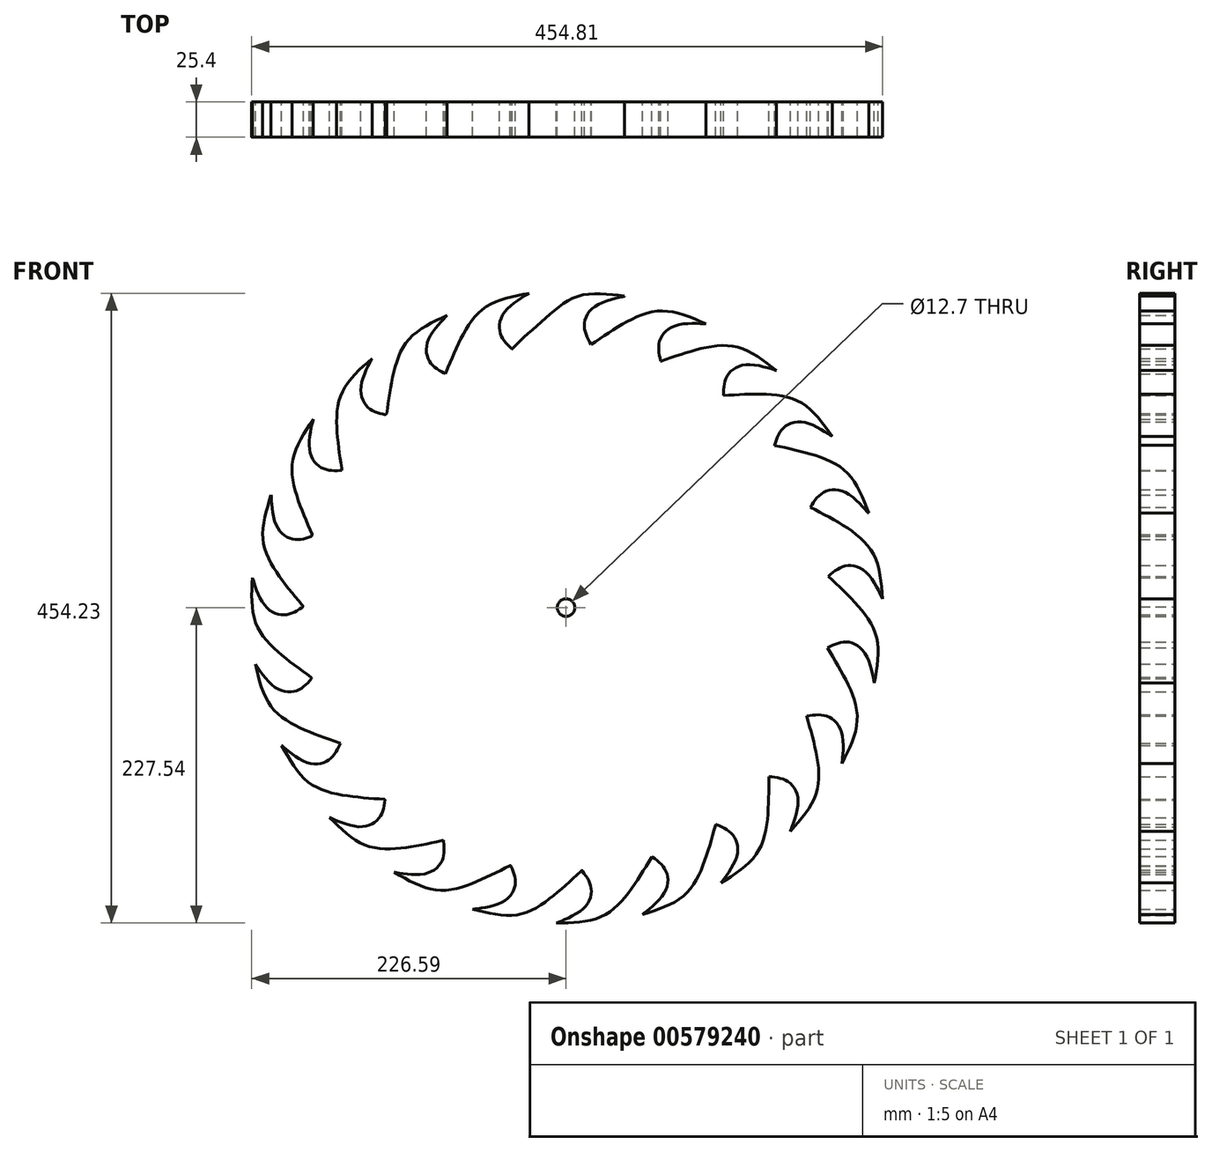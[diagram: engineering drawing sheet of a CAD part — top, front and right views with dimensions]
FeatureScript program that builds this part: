
annotation { "Feature Type Name" : "Feature", "Feature Type Description" : "" }
export const myFeature = defineFeature(function(context is Context, id is Id, definition is map)
    precondition{}
    {
        {
            var Q0;
            Q0=qCreatedBy(makeId("Front.planeOp"),FACE);
            var sketch = newSketch(context, id + "F0", { "sketchPlane" : qUnion([Q0])});
            skCircle(sketch, "E0", {"center": v(0, 0) * mm, "radius": 190.5 * mm});
            skFitSpline(sketch, "E1", {"points": [v(18.12, 189.64) * mm, v(13.24, 202.8) * mm, v(22.46, 218.16) * mm, v(42.19, 224.67) * mm, v(41.34, 224.83) * mm], "startDerivative": vector(-24.64, 44.24) * mm, "endDerivative": vector(-11.68, 1.02) * mm});
            skFitSpline(sketch, "E2", {"points": [v(42.19, 224.67) * mm, v(8.88, 224.67) * mm, v(-15.84, 207.72) * mm, v(-38.7, 186.53) * mm], "startDerivative": vector(-98.7, 12.3) * mm, "endDerivative": vector(-57.4, -63.42) * mm});
            skFitSpline(sketch, "E3", {"points": [v(68.28, 177.66) * mm, v(67.32, 191.67) * mm, v(80.5, 203.8) * mm, v(100.8, 204.7) * mm, v(100.51, 204.86) * mm], "startDerivative": vector(-11.13, 49.4) * mm, "endDerivative": vector(-10.91, 4.28) * mm});
            skFitSpline(sketch, "E4", {"points": [v(100.8, 204.7) * mm, v(69.4, 213.96) * mm, v(42.54, 205.38) * mm, v(18.12, 189.64) * mm], "startDerivative": vector(-91.19, 39.7) * mm, "endDerivative": vector(-72.22, -48.4) * mm});
            skFitSpline(sketch, "E5", {"points": [v(113.46, 153) * mm, v(116.04, 166.8) * mm, v(131.85, 175.23) * mm, v(151.72, 171.01) * mm, v(151.47, 171.23) * mm], "startDerivative": vector(1.62, 50.6) * mm, "endDerivative": vector(-9.49, 6.88) * mm});
            skFitSpline(sketch, "E6", {"points": [v(151.72, 171.01) * mm, v(123.65, 187.84) * mm, v(95.49, 186.28) * mm, v(68.28, 177.66) * mm], "startDerivative": vector(-78.31, 61.3) * mm, "endDerivative": vector(-82.05, -28.74) * mm});
            skFitSpline(sketch, "E7", {"points": [v(150.32, 116.92) * mm, v(156.7, 129.43) * mm, v(174.25, 133.05) * mm, v(192.12, 123.4) * mm, v(191.94, 123.67) * mm], "startDerivative": vector(15.86, 48.09) * mm, "endDerivative": vector(-7.16, 9.28) * mm});
            skFitSpline(sketch, "E8", {"points": [v(192.12, 123.4) * mm, v(169.95, 147.47) * mm, v(142.5, 153.94) * mm, v(113.46, 153) * mm], "startDerivative": vector(-57.79, 80.94) * mm, "endDerivative": vector(-86.83, -4.37) * mm});
            skFitSpline(sketch, "E9", {"points": [v(176.21, 72.44) * mm, v(185.57, 82.91) * mm, v(203.45, 81.95) * mm, v(218.28, 68.06) * mm, v(218.18, 68.38) * mm], "startDerivative": vector(27.57, 42.47) * mm, "endDerivative": vector(-4.56, 10.8) * mm});
            skFitSpline(sketch, "E10", {"points": [v(218.28, 68.06) * mm, v(202.97, 97) * mm, v(178.06, 110.22) * mm, v(150.32, 116.92) * mm], "startDerivative": vector(-35.3, 92.98) * mm, "endDerivative": vector(-85.08, 17.86) * mm});
            skFitSpline(sketch, "E11", {"points": [v(189.1, 22.5) * mm, v(201.03, 29.9) * mm, v(217.92, 23.93) * mm, v(228.22, 6.41) * mm, v(228.21, 6.74) * mm], "startDerivative": vector(38.45, 32.95) * mm, "endDerivative": vector(-1.32, 11.65) * mm});
            skFitSpline(sketch, "E12", {"points": [v(228.22, 6.41) * mm, v(221.7, 38.49) * mm, v(201.55, 58.22) * mm, v(176.21, 72.44) * mm], "startDerivative": vector(-7.57, 99.17) * mm, "endDerivative": vector(-76.56, 41.18) * mm});
            skFitSpline(sketch, "E13", {"points": [v(188.43, -28.96) * mm, v(201.84, -24.8) * mm, v(216.68, -34.81) * mm, v(222.26, -54.35) * mm, v(222.34, -54.03) * mm], "startDerivative": vector(45.48, 22.25) * mm, "endDerivative": vector(1.64, 11.6) * mm});
            skFitSpline(sketch, "E14", {"points": [v(222.26, -54.35) * mm, v(224, -21.67) * mm, v(209.44, 2.49) * mm, v(189.1, 22.5) * mm], "startDerivative": vector(17.54, 97.9) * mm, "endDerivative": vector(-63.79, 59.07) * mm});
            skFitSpline(sketch, "E15", {"points": [v(173.57, -78.3) * mm, v(187.84, -78.2) * mm, v(199.25, -92.02) * mm, v(199.07, -112.34) * mm, v(199.24, -112.05) * mm], "startDerivative": vector(49.92, 8.48) * mm, "endDerivative": vector(4.86, 10.67) * mm});
            skFitSpline(sketch, "E16", {"points": [v(199.07, -112.34) * mm, v(209.98, -81.48) * mm, v(202.85, -54.19) * mm, v(188.43, -28.96) * mm], "startDerivative": vector(44.5, 88.94) * mm, "endDerivative": vector(-44.49, 74.7) * mm});
            skFitSpline(sketch, "E17", {"points": [v(146.3, -121.93) * mm, v(159.9, -125.39) * mm, v(167.32, -141.7) * mm, v(161.85, -161.26) * mm, v(162.08, -161.03) * mm], "startDerivative": vector(50.4, -4.84) * mm, "endDerivative": vector(7.47, 9.03) * mm});
            skFitSpline(sketch, "E18", {"points": [v(161.85, -161.26) * mm, v(180.43, -134.32) * mm, v(180.67, -106.12) * mm, v(173.57, -78.3) * mm], "startDerivative": vector(66.17, 74.25) * mm, "endDerivative": vector(-23.45, 83.71) * mm});
            skFitSpline(sketch, "E19", {"points": [v(107.96, -156.42) * mm, v(120.04, -163.59) * mm, v(122.53, -181.33) * mm, v(111.75, -198.55) * mm, v(112.04, -198.39) * mm], "startDerivative": vector(46.98, -18.89) * mm, "endDerivative": vector(9.72, 6.55) * mm});
            skFitSpline(sketch, "E20", {"points": [v(111.75, -198.55) * mm, v(137.2, -177.96) * mm, v(145.4, -150.97) * mm, v(146.3, -121.93) * mm], "startDerivative": vector(84.46, 52.52) * mm, "endDerivative": vector(1.17, 86.93) * mm});
            skFitSpline(sketch, "E21", {"points": [v(62, -179.6) * mm, v(71.9, -189.56) * mm, v(69.86, -207.36) * mm, v(55.1, -221.33) * mm, v(55.43, -221.25) * mm], "startDerivative": vector(40.74, -30.07) * mm, "endDerivative": vector(11.05, 3.9) * mm});
            skFitSpline(sketch, "E22", {"points": [v(55.1, -221.33) * mm, v(84.9, -207.78) * mm, v(99.6, -183.7) * mm, v(107.96, -156.42) * mm], "startDerivative": vector(94.93, 29.65) * mm, "endDerivative": vector(22.94, 83.86) * mm});
            skFitSpline(sketch, "E23", {"points": [v(11.38, -189.46) * mm, v(18.05, -201.81) * mm, v(11.07, -218.31) * mm, v(-7.03, -227.54) * mm, v(-6.7, -227.55) * mm], "startDerivative": vector(30.58, -40.36) * mm, "endDerivative": vector(11.7, 0.62) * mm});
            skFitSpline(sketch, "E24", {"points": [v(-7.03, -227.54) * mm, v(25.38, -222.97) * mm, v(46.29, -204.04) * mm, v(62, -179.6) * mm], "startDerivative": vector(99.44, 1.6) * mm, "endDerivative": vector(45.7, 73.95) * mm});
            skFitSpline(sketch, "E25", {"points": [v(-39.94, -185.51) * mm, v(-36.63, -199.16) * mm, v(-47.58, -213.34) * mm, v(-67.43, -217.66) * mm, v(-67.12, -217.75) * mm], "startDerivative": vector(19.3, -46.8) * mm, "endDerivative": vector(11.48, -2.38) * mm});
            skFitSpline(sketch, "E26", {"points": [v(-67.43, -217.66) * mm, v(-34.92, -221.48) * mm, v(-9.89, -208.49) * mm, v(11.38, -189.46) * mm], "startDerivative": vector(96.58, -23.74) * mm, "endDerivative": vector(63.02, 59.9) * mm});
            skFitSpline(sketch, "E27", {"points": [v(-88.36, -167.76) * mm, v(-89.05, -181.79) * mm, v(-103.56, -192.3) * mm, v(-123.82, -190.82) * mm, v(-123.54, -191) * mm], "startDerivative": vector(5.29, -50.36) * mm, "endDerivative": vector(10.34, -5.53) * mm});
            skFitSpline(sketch, "E28", {"points": [v(-123.82, -190.82) * mm, v(-93.72, -203.68) * mm, v(-66.03, -198.3) * mm, v(-40.25, -186.06) * mm], "startDerivative": vector(85.93, -50.08) * mm, "endDerivative": vector(77.38, 39.64) * mm});
            skFitSpline(sketch, "E29", {"points": [v(-130.35, -137.99) * mm, v(-134.53, -151.4) * mm, v(-151.2, -157.92) * mm, v(-170.45, -151.42) * mm, v(-170.23, -151.66) * mm], "startDerivative": vector(-7.52, -50.07) * mm, "endDerivative": vector(8.62, -7.94) * mm});
            skFitSpline(sketch, "E30", {"points": [v(-170.45, -151.42) * mm, v(-144.54, -171.4) * mm, v(-116.39, -173.15) * mm, v(-88.36, -167.76) * mm], "startDerivative": vector(70.62, -70.03) * mm, "endDerivative": vector(84.84, 18.96) * mm});
            skFitSpline(sketch, "E31", {"points": [v(-162.75, -97.86) * mm, v(-170.55, -109.54) * mm, v(-188.4, -111.09) * mm, v(-205.02, -99.4) * mm, v(-204.87, -99.7) * mm], "startDerivative": vector(-21.36, -45.9) * mm, "endDerivative": vector(6.02, -10.06) * mm});
            skFitSpline(sketch, "E32", {"points": [v(-205.02, -99.4) * mm, v(-185.81, -125.91) * mm, v(-159.3, -135.53) * mm, v(-130.9, -138.3) * mm], "startDerivative": vector(47.94, -87.14) * mm, "endDerivative": vector(86.74, -5.8) * mm});
            skFitSpline(sketch, "E33", {"points": [v(-182.85, -50.48) * mm, v(-193.45, -59.7) * mm, v(-211.07, -56.5) * mm, v(-224.04, -40.86) * mm, v(-223.98, -41.19) * mm], "startDerivative": vector(-32.68, -38.68) * mm, "endDerivative": vector(3.17, -11.28) * mm});
            skFitSpline(sketch, "E34", {"points": [v(-224.04, -40.86) * mm, v(-212.48, -71.48) * mm, v(-189.43, -87.73) * mm, v(-162.75, -97.86) * mm], "startDerivative": vector(23.36, -96.68) * mm, "endDerivative": vector(82.17, -28.4) * mm});
            skFitSpline(sketch, "E35", {"points": [v(-189.38, 0.68) * mm, v(-202.14, -5.17) * mm, v(-218.15, 2.88) * mm, v(-226.17, 21.55) * mm, v(-226.2, 21.22) * mm], "startDerivative": vector(-42.28, -27.86) * mm, "endDerivative": vector(-0.15, -11.72) * mm});
            skFitSpline(sketch, "E36", {"points": [v(-226.17, 21.55) * mm, v(-223.73, -11.1) * mm, v(-206.21, -33.2) * mm, v(-183.48, -50.45) * mm], "startDerivative": vector(-4.93, -99.33) * mm, "endDerivative": vector(70.8, -50.46) * mm});
            skFitSpline(sketch, "E37", {"points": [v(-182.26, 51.65) * mm, v(-196.08, 49.2) * mm, v(-209.55, 61) * mm, v(-212.63, 81.09) * mm, v(-212.75, 80.78) * mm], "startDerivative": vector(-47.92, -16.37) * mm, "endDerivative": vector(-3.09, -11.3) * mm});
            skFitSpline(sketch, "E38", {"points": [v(-212.63, 81.09) * mm, v(-218.46, 48.88) * mm, v(-207.05, 23.09) * mm, v(-189.38, 0.68) * mm], "startDerivative": vector(-29.69, -94.92) * mm, "endDerivative": vector(55.87, -66.6) * mm});
            skFitSpline(sketch, "E39", {"points": [v(-161.54, 98.88) * mm, v(-175.5, 100.44) * mm, v(-185.08, 115.57) * mm, v(-182.36, 135.7) * mm, v(-182.56, 135.44) * mm], "startDerivative": vector(-50.59, -2.15) * mm, "endDerivative": vector(-6.16, -9.97) * mm});
            skFitSpline(sketch, "E40", {"points": [v(-182.36, 135.7) * mm, v(-197.05, 106.46) * mm, v(-193.4, 78.49) * mm, v(-182.78, 52) * mm], "startDerivative": vector(-55.3, -82.66) * mm, "endDerivative": vector(34.77, -79.68) * mm});
            skFitSpline(sketch, "E41", {"points": [v(-129.07, 138.82) * mm, v(-142.17, 143.87) * mm, v(-147.6, 160.95) * mm, v(-139.84, 179.73) * mm, v(-140.1, 179.52) * mm], "startDerivative": vector(-49.47, 10.79) * mm, "endDerivative": vector(-8.5, -8.08) * mm});
            skFitSpline(sketch, "E42", {"points": [v(-139.84, 179.73) * mm, v(-161.5, 155.18) * mm, v(-165.07, 127.2) * mm, v(-161.54, 98.88) * mm], "startDerivative": vector(-74.52, -65.87) * mm, "endDerivative": vector(13.35, -85.9) * mm});
            skFitSpline(sketch, "E43", {"points": [v(-86.9, 168.52) * mm, v(-98.05, 177.07) * mm, v(-98.42, 194.98) * mm, v(-85.67, 210.8) * mm, v(-85.98, 210.68) * mm], "startDerivative": vector(-44.4, 24.33) * mm, "endDerivative": vector(-10.43, -5.35) * mm});
            skFitSpline(sketch, "E44", {"points": [v(-85.67, 210.8) * mm, v(-113.38, 193.38) * mm, v(-124.72, 167.55) * mm, v(-129.34, 139.39) * mm], "startDerivative": vector(-90.1, -42.12) * mm, "endDerivative": vector(-11.48, -86.18) * mm});
            skFitSpline(sketch, "E45", {"points": [v(-38.52, 186.08) * mm, v(-47.16, 197.15) * mm, v(-43.03, 214.58) * mm, v(-26.72, 226.7) * mm, v(-27.05, 226.65) * mm], "startDerivative": vector(-36.88, 34.7) * mm, "endDerivative": vector(-11.44, -2.56) * mm});
            skFitSpline(sketch, "E46", {"points": [v(-26.72, 226.7) * mm, v(-57.92, 216.78) * mm, v(-75.37, 194.62) * mm, v(-86.9, 168.52) * mm], "startDerivative": vector(-97.78, -18.17) * mm, "endDerivative": vector(-32.73, -80.54) * mm});
            skCircle(sketch, "E47", {"center": v(0, 0) * mm, "radius": 6.35 * mm});
            skSolve(sketch);
        }
        {
            var Q0;
            {var subQ0=sQuery(id+"F0.wireOp",EDGE,"E33");var subQ1=sQuery(id+"F0.wireOp",EDGE,"E0");var subQ2=makeQuery(id+"F0.imprint","INTERSECT",VERTEX,{"derivedFrom":[subQ1,subQ0]});Q0=makeQuery(id+"F0.imprint","IMPRINT",FACE,{"disambiguationData":[TD([[makeQuery(id+"F0.imprint","IMPRINT",EDGE,{"disambiguationData":[TD([[subQ2,-1.0]])],"derivedFrom":subQ1}),-1.0]])]});}
            var Q1;
            {var subQ0=sQuery(id+"F0.wireOp",EDGE,"E36");var subQ1=sQuery(id+"F0.wireOp",EDGE,"E0");var subQ2=makeQuery(id+"F0.imprint","INTERSECT",VERTEX,{"derivedFrom":[subQ1,subQ0]});Q1=makeQuery(id+"F0.imprint","IMPRINT",FACE,{"disambiguationData":[TD([[makeQuery(id+"F0.imprint","IMPRINT",EDGE,{"disambiguationData":[TD([[subQ2,1.0]])],"derivedFrom":subQ1}),-1.0]])]});}
            var Q2;
            {var subQ0=sQuery(id+"F0.wireOp",EDGE,"E37");var subQ1=sQuery(id+"F0.wireOp",EDGE,"E0");var subQ2=makeQuery(id+"F0.imprint","INTERSECT",VERTEX,{"derivedFrom":[subQ1,subQ0]});Q2=makeQuery(id+"F0.imprint","IMPRINT",FACE,{"disambiguationData":[TD([[makeQuery(id+"F0.imprint","IMPRINT",EDGE,{"disambiguationData":[TD([[subQ2,-1.0]])],"derivedFrom":subQ1}),-1.0]])]});}
            var Q3;
            {var subQ0=sQuery(id+"F0.wireOp",EDGE,"E40");var subQ1=sQuery(id+"F0.wireOp",EDGE,"E0");var subQ2=makeQuery(id+"F0.imprint","INTERSECT",VERTEX,{"derivedFrom":[subQ1,subQ0]});Q3=makeQuery(id+"F0.imprint","IMPRINT",FACE,{"disambiguationData":[TD([[makeQuery(id+"F0.imprint","IMPRINT",EDGE,{"disambiguationData":[TD([[subQ2,1.0]])],"derivedFrom":subQ1}),-1.0]])]});}
            var Q4;
            {var subQ0=sQuery(id+"F0.wireOp",EDGE,"E41");var subQ1=sQuery(id+"F0.wireOp",EDGE,"E0");var subQ2=makeQuery(id+"F0.imprint","INTERSECT",VERTEX,{"derivedFrom":[subQ1,subQ0]});Q4=makeQuery(id+"F0.imprint","IMPRINT",FACE,{"disambiguationData":[TD([[makeQuery(id+"F0.imprint","IMPRINT",EDGE,{"disambiguationData":[TD([[subQ2,-1.0]])],"derivedFrom":subQ1}),-1.0]])]});}
            var Q5;
            {var subQ0=sQuery(id+"F0.wireOp",EDGE,"E32");var subQ1=sQuery(id+"F0.wireOp",EDGE,"E0");var subQ2=makeQuery(id+"F0.imprint","INTERSECT",VERTEX,{"derivedFrom":[subQ1,subQ0]});Q5=makeQuery(id+"F0.imprint","IMPRINT",FACE,{"disambiguationData":[TD([[makeQuery(id+"F0.imprint","IMPRINT",EDGE,{"disambiguationData":[TD([[subQ2,1.0]])],"derivedFrom":subQ1}),-1.0]])]});}
            var Q6;
            {var subQ0=sQuery(id+"F0.wireOp",EDGE,"E29");var subQ1=sQuery(id+"F0.wireOp",EDGE,"E0");var subQ2=makeQuery(id+"F0.imprint","INTERSECT",VERTEX,{"derivedFrom":[subQ1,subQ0]});Q6=makeQuery(id+"F0.imprint","IMPRINT",FACE,{"disambiguationData":[TD([[makeQuery(id+"F0.imprint","IMPRINT",EDGE,{"disambiguationData":[TD([[subQ2,-1.0]])],"derivedFrom":subQ1}),-1.0]])]});}
            var Q7;
            {var subQ0=sQuery(id+"F0.wireOp",EDGE,"E28");var subQ1=sQuery(id+"F0.wireOp",EDGE,"E0");var subQ2=makeQuery(id+"F0.imprint","INTERSECT",VERTEX,{"derivedFrom":[subQ1,subQ0]});Q7=makeQuery(id+"F0.imprint","IMPRINT",FACE,{"disambiguationData":[TD([[makeQuery(id+"F0.imprint","IMPRINT",EDGE,{"disambiguationData":[TD([[subQ2,1.0]])],"derivedFrom":subQ1}),-1.0]])]});}
            var Q8;
            {var subQ0=sQuery(id+"F0.wireOp",EDGE,"E25");var subQ1=sQuery(id+"F0.wireOp",EDGE,"E0");var subQ2=makeQuery(id+"F0.imprint","INTERSECT",VERTEX,{"derivedFrom":[subQ1,subQ0]});Q8=makeQuery(id+"F0.imprint","IMPRINT",FACE,{"disambiguationData":[TD([[makeQuery(id+"F0.imprint","IMPRINT",EDGE,{"disambiguationData":[TD([[subQ2,-1.0]])],"derivedFrom":subQ1}),-1.0]])]});}
            var Q9;
            {var subQ0=sQuery(id+"F0.wireOp",EDGE,"E23");var subQ1=sQuery(id+"F0.wireOp",EDGE,"E0");var subQ2=makeQuery(id+"F0.imprint","INTERSECT",VERTEX,{"derivedFrom":[subQ1,subQ0]});Q9=makeQuery(id+"F0.imprint","IMPRINT",FACE,{"disambiguationData":[TD([[makeQuery(id+"F0.imprint","IMPRINT",EDGE,{"disambiguationData":[TD([[subQ2,-1.0]])],"derivedFrom":subQ1}),-1.0]])]});}
            var Q10;
            {var subQ0=sQuery(id+"F0.wireOp",EDGE,"E21");var subQ1=sQuery(id+"F0.wireOp",EDGE,"E0");var subQ2=makeQuery(id+"F0.imprint","INTERSECT",VERTEX,{"derivedFrom":[subQ1,subQ0]});Q10=makeQuery(id+"F0.imprint","IMPRINT",FACE,{"disambiguationData":[TD([[makeQuery(id+"F0.imprint","IMPRINT",EDGE,{"disambiguationData":[TD([[subQ2,-1.0]])],"derivedFrom":subQ1}),-1.0]])]});}
            var Q11;
            {var subQ0=sQuery(id+"F0.wireOp",EDGE,"E19");var subQ1=sQuery(id+"F0.wireOp",EDGE,"E0");var subQ2=makeQuery(id+"F0.imprint","INTERSECT",VERTEX,{"derivedFrom":[subQ1,subQ0]});Q11=makeQuery(id+"F0.imprint","IMPRINT",FACE,{"disambiguationData":[TD([[makeQuery(id+"F0.imprint","IMPRINT",EDGE,{"disambiguationData":[TD([[subQ2,-1.0]])],"derivedFrom":subQ1}),-1.0]])]});}
            var Q12;
            {var subQ0=sQuery(id+"F0.wireOp",EDGE,"E17");var subQ1=sQuery(id+"F0.wireOp",EDGE,"E0");var subQ2=makeQuery(id+"F0.imprint","INTERSECT",VERTEX,{"derivedFrom":[subQ1,subQ0]});Q12=makeQuery(id+"F0.imprint","IMPRINT",FACE,{"disambiguationData":[TD([[makeQuery(id+"F0.imprint","IMPRINT",EDGE,{"disambiguationData":[TD([[subQ2,-1.0]])],"derivedFrom":subQ1}),-1.0]])]});}
            var Q13;
            {var subQ0=sQuery(id+"F0.wireOp",EDGE,"E7");var subQ1=sQuery(id+"F0.wireOp",EDGE,"E0");var subQ2=makeQuery(id+"F0.imprint","INTERSECT",VERTEX,{"derivedFrom":[subQ1,subQ0]});Q13=makeQuery(id+"F0.imprint","IMPRINT",FACE,{"disambiguationData":[TD([[makeQuery(id+"F0.imprint","IMPRINT",EDGE,{"disambiguationData":[TD([[subQ2,-1.0]])],"derivedFrom":subQ1}),-1.0]])]});}
            var Q14;
            {var subQ0=sQuery(id+"F0.wireOp",EDGE,"E5");var subQ1=sQuery(id+"F0.wireOp",EDGE,"E0");var subQ2=makeQuery(id+"F0.imprint","INTERSECT",VERTEX,{"derivedFrom":[subQ1,subQ0]});Q14=makeQuery(id+"F0.imprint","IMPRINT",FACE,{"disambiguationData":[TD([[makeQuery(id+"F0.imprint","IMPRINT",EDGE,{"disambiguationData":[TD([[subQ2,-1.0]])],"derivedFrom":subQ1}),-1.0]])]});}
            var Q15;
            {var subQ0=sQuery(id+"F0.wireOp",EDGE,"E4");Q15=makeQuery(id+"F0.imprint","IMPRINT",FACE,{"disambiguationData":[TD([[makeQuery(id+"F0.imprint","IMPRINT",EDGE,{"derivedFrom":subQ0}),1.0]])]});}
            var Q16;
            {var subQ3=sQuery(id+"F0.wireOp",EDGE,"E2");Q16=makeQuery(id+"F0.imprint","IMPRINT",FACE,{"disambiguationData":[TD([[makeQuery(id+"F0.imprint","IMPRINT",EDGE,{"derivedFrom":subQ3}),1.0]])]});}
            var Q17;
            {var subQ0=sQuery(id+"F0.wireOp",EDGE,"E45");var subQ1=sQuery(id+"F0.wireOp",EDGE,"E0");var subQ2=makeQuery(id+"F0.imprint","INTERSECT",VERTEX,{"derivedFrom":[subQ1,subQ0]});Q17=makeQuery(id+"F0.imprint","IMPRINT",FACE,{"disambiguationData":[TD([[makeQuery(id+"F0.imprint","IMPRINT",EDGE,{"disambiguationData":[TD([[subQ2,-1.0]])],"derivedFrom":subQ1}),-1.0]])]});}
            var Q18;
            {var subQ0=sQuery(id+"F0.wireOp",EDGE,"E44");var subQ1=sQuery(id+"F0.wireOp",EDGE,"E0");var subQ2=makeQuery(id+"F0.imprint","INTERSECT",VERTEX,{"derivedFrom":[subQ1,subQ0]});Q18=makeQuery(id+"F0.imprint","IMPRINT",FACE,{"disambiguationData":[TD([[makeQuery(id+"F0.imprint","IMPRINT",EDGE,{"disambiguationData":[TD([[subQ2,1.0]])],"derivedFrom":subQ1}),-1.0]])]});}
            var Q19;
            {var subQ0=sQuery(id+"F0.wireOp",EDGE,"E12");Q19=makeQuery(id+"F0.imprint","IMPRINT",FACE,{"disambiguationData":[TD([[makeQuery(id+"F0.imprint","IMPRINT",EDGE,{"derivedFrom":subQ0}),1.0]])]});}
            var Q20;
            {var subQ0=sQuery(id+"F0.wireOp",EDGE,"E16");Q20=makeQuery(id+"F0.imprint","IMPRINT",FACE,{"disambiguationData":[TD([[makeQuery(id+"F0.imprint","IMPRINT",EDGE,{"derivedFrom":subQ0}),1.0]])]});}
            var Q21;
            Q21=makeQuery(id+"F0.imprint","IMPRINT",FACE,{"disambiguationData":[TD([[makeQuery(id+"F0.imprint","IMPRINT",EDGE,{"derivedFrom":sQuery(id+"F0.wireOp",EDGE,"E47")}),-1.0]])]});
            extrude(context, id + "F1", {"entities" : qUnion([Q0, Q1, Q2, Q3, Q4, Q5, Q6, Q7, Q8, Q9, Q10, Q11, Q12, Q13, Q14, Q15, Q16, Q17, Q18, Q19, Q20, Q21]), "depth" : 25.4 * mm, "offsetDistance" : 25.4 * mm});
        }
    });
